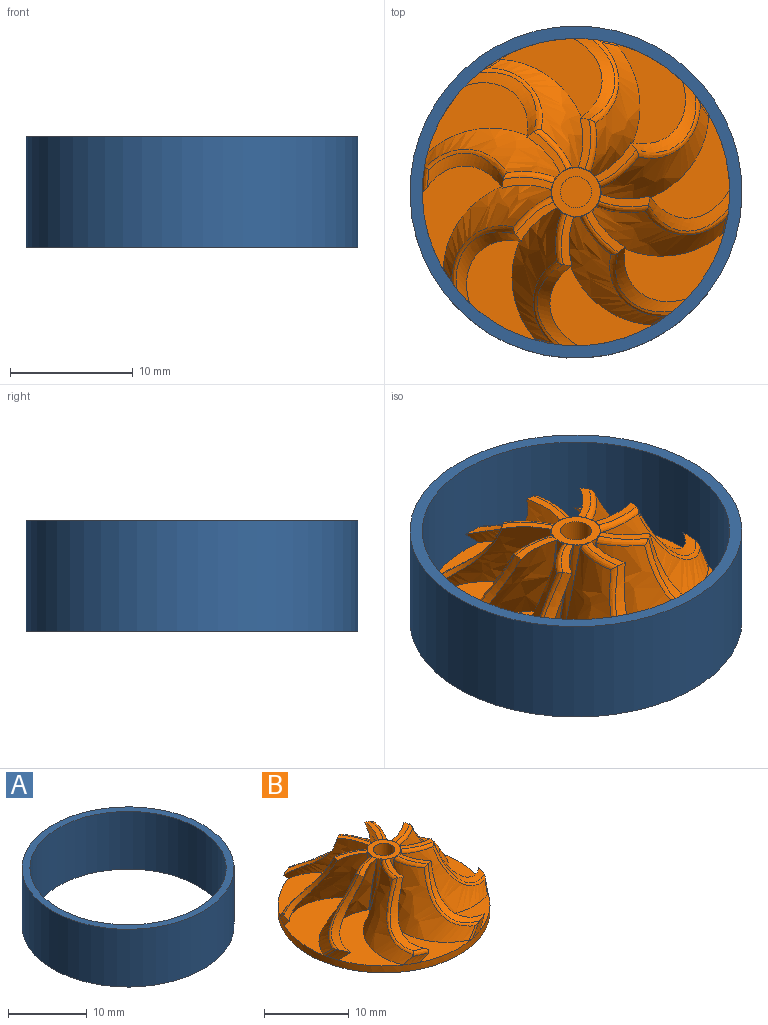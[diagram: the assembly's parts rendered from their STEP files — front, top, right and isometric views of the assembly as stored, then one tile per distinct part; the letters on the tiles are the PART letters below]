
ASSEMBLY  parts=2 mates=1
PART A: 4 faces, bbox 27x27x9 mm
  f0: cylinder r=12.5mm len=25mm, axis (0,0,-1), area 706.9mm2, adj f2,f3
  f1: cylinder r=13.5mm len=27mm, axis (0,0,-1), area 763.4mm2, adj f2,f3
  f2: plane 27x27mm, normal (0,0,1), area 81.7mm2, adj f0,f1
  f3: plane 27x27mm, normal (0,0,-1), area 81.7mm2, adj f0,f1
PART B: 126 faces, bbox 25.5x25.7x12.8 mm
  f0: bspline ~5.71x1.48mm, area 0mm2, adj f1,f120,f121,f125
  f1: plane 4.27x2.35mm, normal (0,0,1), area 2.6mm2, adj f0,f2,f118,f119,f125
  f2: bspline ~13.95x11.52mm, area 64.8mm2, adj f1,f3,f117,f118,f125
  f3: plane 11.93x9.66mm, normal (0,0,1), area 46.9mm2, adj f2,f4,f112,f113,f114,f115,f125
  f4: cylinder r=2mm len=7.98mm, axis (0,0,-1), area 4.5mm2, adj f3,f5,f111,f112,f121,f125
  f5: bspline ~0.5x0.42mm, area 0mm2, adj f4,f6,f110
  f6: bspline ~6.43x2.47mm, area 2.6mm2, adj f5,f7,f108,f109,f111,f113
  f7: bspline ~8.68x7.14mm, area 4.9mm2, adj f6,f8,f109,f113,f114
  f8: bspline ~6.6x5.71mm, area 2.6mm2, adj f7,f9,f109,f114,f115
  f9: bspline ~14.97x11.43mm, area 64.8mm2, adj f8,f10,f107,f108,f109
  f10: bspline ~11.43x1.76mm, area 0.5mm2, adj f9,f11,f107,f108,f110
  f11: cylinder r=2mm len=7.98mm, axis (0,0,-1), area 4.5mm2, adj f10,f12,f105,f106,f107,f121
  f12: bspline ~0.42x0.39mm, area 0mm2, adj f11,f13,f104
  f13: bspline ~6.05x3.39mm, area 2.6mm2, adj f12,f14,f101,f102,f103,f105
  f14: bspline ~8.68x6.88mm, area 4.9mm2, adj f13,f15,f16,f101,f103
  f15: bspline ~3.56x3mm, area 0.7mm2, adj f14,f16,f101,f107
  f16: bspline ~7.15x5.71mm, area 2.6mm2, adj f14,f15,f17,f103,f115
  f17: bspline ~13.95x11.52mm, area 64.8mm2, adj f16,f18,f100,f102,f103
  f18: bspline ~11.43x1.49mm, area 0.5mm2, adj f17,f19,f100,f102,f104
  f19: cylinder r=2mm len=7.98mm, axis (0,0,-1), area 4.5mm2, adj f18,f20,f98,f99,f100,f121
  f20: bspline ~0.5x0.42mm, area 0mm2, adj f19,f21,f97
  f21: bspline ~6.43x2.47mm, area 2.6mm2, adj f20,f22,f94,f95,f96,f98
  f22: bspline ~8.68x7.14mm, area 4.9mm2, adj f21,f23,f24,f94,f96
  f23: bspline ~3.56x3.41mm, area 0.7mm2, adj f22,f24,f94,f100
  f24: bspline ~6.6x5.71mm, area 2.6mm2, adj f22,f23,f25,f96,f115
  f25: bspline ~14.97x11.43mm, area 64.8mm2, adj f24,f26,f93,f95,f96
  f26: bspline ~11.43x1.76mm, area 0.5mm2, adj f25,f27,f93,f95,f97
  f27: cylinder r=2mm len=7.98mm, axis (0,0,-1), area 4.5mm2, adj f26,f28,f91,f92,f93,f121
  f28: bspline ~0.42x0.39mm, area 0mm2, adj f27,f29,f90
  f29: bspline ~6.05x3.39mm, area 2.6mm2, adj f28,f30,f87,f88,f89,f91
  f30: bspline ~8.68x6.88mm, area 4.9mm2, adj f29,f31,f32,f87,f89
  f31: bspline ~3.56x3mm, area 0.7mm2, adj f30,f32,f87,f93
  f32: bspline ~7.15x5.71mm, area 2.6mm2, adj f30,f31,f33,f89,f115
  f33: bspline ~13.95x11.52mm, area 64.8mm2, adj f32,f34,f86,f88,f89
  f34: bspline ~11.43x1.49mm, area 0.5mm2, adj f33,f35,f86,f88,f90
  f35: cylinder r=2mm len=7.98mm, axis (0,0,-1), area 4.5mm2, adj f34,f36,f84,f85,f86,f121
  f36: bspline ~0.5x0.42mm, area 0mm2, adj f35,f37,f83
  f37: bspline ~6.43x2.47mm, area 2.6mm2, adj f36,f38,f80,f81,f82,f84
  f38: bspline ~8.68x7.14mm, area 4.9mm2, adj f37,f39,f40,f80,f82
  f39: bspline ~3.56x3.41mm, area 0.7mm2, adj f38,f40,f80,f86
  f40: bspline ~6.6x5.71mm, area 2.6mm2, adj f38,f39,f41,f82,f115
  f41: bspline ~14.97x11.43mm, area 64.8mm2, adj f40,f42,f79,f81,f82
  f42: bspline ~11.43x1.76mm, area 0.5mm2, adj f41,f43,f79,f81,f83
  f43: cylinder r=2mm len=7.98mm, axis (0,0,-1), area 4.5mm2, adj f42,f44,f77,f78,f79,f121
  f44: bspline ~0.42x0.39mm, area 0mm2, adj f43,f45,f76
  f45: bspline ~6.05x3.39mm, area 2.6mm2, adj f44,f46,f73,f74,f75,f77
  f46: bspline ~8.65x6.31mm, area 4.7mm2, adj f45,f47,f73,f75
  f47: bspline ~2.43x1.4mm, area 1.3mm2, adj f46,f48,f49,f73,f75
  f48: bspline ~7.15x5.71mm, area 2.1mm2, adj f47,f49,f73,f115
  f49: bspline ~13.95x11.52mm, area 64.6mm2, adj f47,f48,f50,f72,f74,f75
  f50: bspline ~11.43x1.49mm, area 0.5mm2, adj f49,f51,f72,f74,f76
  f51: cylinder r=2mm len=7.98mm, axis (0,0,-1), area 4.5mm2, adj f50,f52,f70,f71,f72,f121
  f52: bspline ~0.5x0.42mm, area 0mm2, adj f51,f53,f69
  f53: bspline ~6.43x2.47mm, area 2.6mm2, adj f52,f54,f66,f67,f68,f70
  f54: bspline ~8.68x7.14mm, area 4.9mm2, adj f53,f55,f56,f66,f68
  f55: bspline ~3.56x3.41mm, area 0.7mm2, adj f54,f56,f66,f72
  f56: bspline ~6.6x5.71mm, area 2.6mm2, adj f54,f55,f57,f68,f115
  f57: bspline ~14.97x11.43mm, area 64.8mm2, adj f56,f58,f65,f67,f68
  f58: bspline ~11.43x1.76mm, area 0.5mm2, adj f57,f59,f65,f67,f69
  f59: cylinder r=2mm len=7.98mm, axis (0,0,-1), area 4.5mm2, adj f58,f60,f61,f65,f120,f121
  f60: bspline ~0.43x0.43mm, area 0mm2, adj f59,f61,f119
  f61: bspline ~11.43x1.62mm, area 0.5mm2, adj f59,f60,f62,f65
  f62: bspline ~12.33x7.69mm, area 62mm2, adj f61,f63,f64,f65,f119
  f63: bspline ~3.56x3mm, area 0.7mm2, adj f62,f64,f65,f117
  f64: bspline ~8.68x6.88mm, area 4.9mm2, adj f62,f63,f117,f118,f119
  f65: plane 12.33x10.25mm, normal (0,0,1), area 46.9mm2, adj f57,f58,f59,f61,f62,f63,f115
  f66: bspline ~14.95x11.43mm, area 62mm2, adj f53,f54,f55,f71,f72
  f67: plane 4.13x2.38mm, normal (0,0,1), area 2.6mm2, adj f53,f57,f58,f68,f69
  f68: revolved ~7.08x6.5mm, area 9.9mm2, adj f53,f54,f56,f57,f67
  f69: bspline ~5.71x1.82mm, area 0mm2, adj f52,f58,f67,f121
  f70: bspline ~0.5x0.43mm, area 0mm2, adj f51,f53,f71
  f71: bspline ~11.43x1.7mm, area 0.5mm2, adj f51,f66,f70,f72
  f72: plane 11.93x9.66mm, normal (0,0,1), area 46.9mm2, adj f49,f50,f51,f55,f66,f71,f115
  f73: bspline ~12.75x12.67mm, area 62.4mm2, adj f45,f46,f47,f48,f78,f79
  f74: plane 4.27x2.35mm, normal (0,0,1), area 2.6mm2, adj f45,f49,f50,f75,f76
  f75: revolved ~6.65x6.44mm, area 9.3mm2, adj f45,f46,f47,f49,f74
  f76: bspline ~5.71x1.48mm, area 0mm2, adj f44,f50,f74,f121
  f77: bspline ~0.43x0.43mm, area 0mm2, adj f43,f45,f78
  f78: bspline ~11.43x1.62mm, area 0.5mm2, adj f43,f73,f77,f79
  f79: plane 12.18x10.25mm, normal (0,0,1), area 46.9mm2, adj f41,f42,f43,f73,f78,f115
  f80: bspline ~14.95x11.43mm, area 62mm2, adj f37,f38,f39,f85,f86
  f81: plane 4.13x2.38mm, normal (0,0,1), area 2.6mm2, adj f37,f41,f42,f82,f83
  f82: revolved ~7.08x6.5mm, area 9.9mm2, adj f37,f38,f40,f41,f81
  f83: bspline ~5.71x1.82mm, area 0mm2, adj f36,f42,f81,f121
  f84: bspline ~0.5x0.43mm, area 0mm2, adj f35,f37,f85
  f85: bspline ~11.43x1.7mm, area 0.5mm2, adj f35,f80,f84,f86
  f86: plane 11.93x9.66mm, normal (0,0,1), area 46.9mm2, adj f33,f34,f35,f39,f80,f85,f115
  f87: bspline ~12.33x7.69mm, area 62mm2, adj f29,f30,f31,f92,f93
  f88: plane 4.27x2.35mm, normal (0,0,1), area 2.6mm2, adj f29,f33,f34,f89,f90
  f89: revolved ~7.26x6.5mm, area 9.9mm2, adj f29,f30,f32,f33,f88
  f90: bspline ~5.71x1.48mm, area 0mm2, adj f28,f34,f88,f121
  f91: bspline ~0.43x0.43mm, area 0mm2, adj f27,f29,f92
  f92: bspline ~11.43x1.62mm, area 0.5mm2, adj f27,f87,f91,f93
  f93: plane 12.33x10.25mm, normal (0,0,1), area 46.9mm2, adj f25,f26,f27,f31,f87,f92,f115
  f94: bspline ~14.95x11.43mm, area 62mm2, adj f21,f22,f23,f99,f100
  f95: plane 4.13x2.38mm, normal (0,0,1), area 2.6mm2, adj f21,f25,f26,f96,f97
  f96: revolved ~7.08x6.5mm, area 9.9mm2, adj f21,f22,f24,f25,f95
  f97: bspline ~5.71x1.82mm, area 0mm2, adj f20,f26,f95,f121
  f98: bspline ~0.5x0.43mm, area 0mm2, adj f19,f21,f99
  f99: bspline ~11.43x1.7mm, area 0.5mm2, adj f19,f94,f98,f100
  f100: plane 11.93x9.66mm, normal (0,0,1), area 46.9mm2, adj f17,f18,f19,f23,f94,f99,f115
  f101: bspline ~12.33x7.69mm, area 62mm2, adj f13,f14,f15,f106,f107
  f102: plane 4.27x2.35mm, normal (0,0,1), area 2.6mm2, adj f13,f17,f18,f103,f104
  f103: revolved ~7.26x6.5mm, area 9.9mm2, adj f13,f14,f16,f17,f102
  f104: bspline ~5.71x1.48mm, area 0mm2, adj f12,f18,f102,f121
  f105: bspline ~0.43x0.43mm, area 0mm2, adj f11,f13,f106
  f106: bspline ~11.43x1.62mm, area 0.5mm2, adj f11,f101,f105,f107
  f107: plane 12.33x10.25mm, normal (0,0,1), area 46.9mm2, adj f9,f10,f11,f15,f101,f106,f115
  f108: plane 4.13x2.38mm, normal (0,0,1), area 2.6mm2, adj f6,f9,f10,f109,f110
  f109: revolved ~7.08x6.5mm, area 9.9mm2, adj f6,f7,f8,f9,f108
  f110: bspline ~5.71x1.82mm, area 0mm2, adj f5,f10,f108,f121
  f111: bspline ~0.5x0.43mm, area 0mm2, adj f4,f6,f112
  f112: bspline ~11.43x1.7mm, area 0.5mm2, adj f3,f4,f111,f113
  f113: bspline ~14.95x11.43mm, area 62mm2, adj f3,f6,f7,f112,f114
  f114: bspline ~3.56x3.41mm, area 0.7mm2, adj f3,f7,f8,f113
  f115: cylinder r=12.5mm len=25mm, axis (0,0,1), area 78.5mm2, adj f3,f8,f16,f24,f32,f40,f48,f56
  f116: plane 25x25mm, normal (0,0,-1), area 490.9mm2, adj f115
  f117: bspline ~7.15x5.71mm, area 2.6mm2, adj f2,f63,f64,f115,f118
  f118: revolved ~7.26x6.5mm, area 9.9mm2, adj f1,f2,f64,f117,f119
  f119: bspline ~6.05x3.39mm, area 2.6mm2, adj f1,f60,f62,f64,f118,f120
  f120: bspline ~0.42x0.39mm, area 0mm2, adj f0,f59,f119
  f121: torus R=1.98mm, axis (0,0,1), area 0.5mm2, adj f0,f4,f11,f19,f27,f35,f43,f51
  f122: plane 3.95x3.95mm, normal (0,0,1), area 7.2mm2, adj f121,f123
  f123: cylinder r=1.27mm len=8mm, axis (0,0,-1), area 63.8mm2, adj f122,f124
  f124: plane 2.54x2.54mm, normal (0,0,1), area 5.1mm2, adj f123
  f125: bspline ~11.43x1.49mm, area 0.5mm2, adj f0,f1,f2,f3,f4
PLACE A rot(axis=(0,0,1),19.6deg) t=(-22.34,-9.34,-15.74)mm
PLACE B rot(axis=(0,0,-1),70.4deg) t=(-22.34,-9.34,-14.74)mm
MATE revolute A.f1 <-> B.f115  axis (0,0,-1) through (-22.34,-9.34,-15.74)mm
